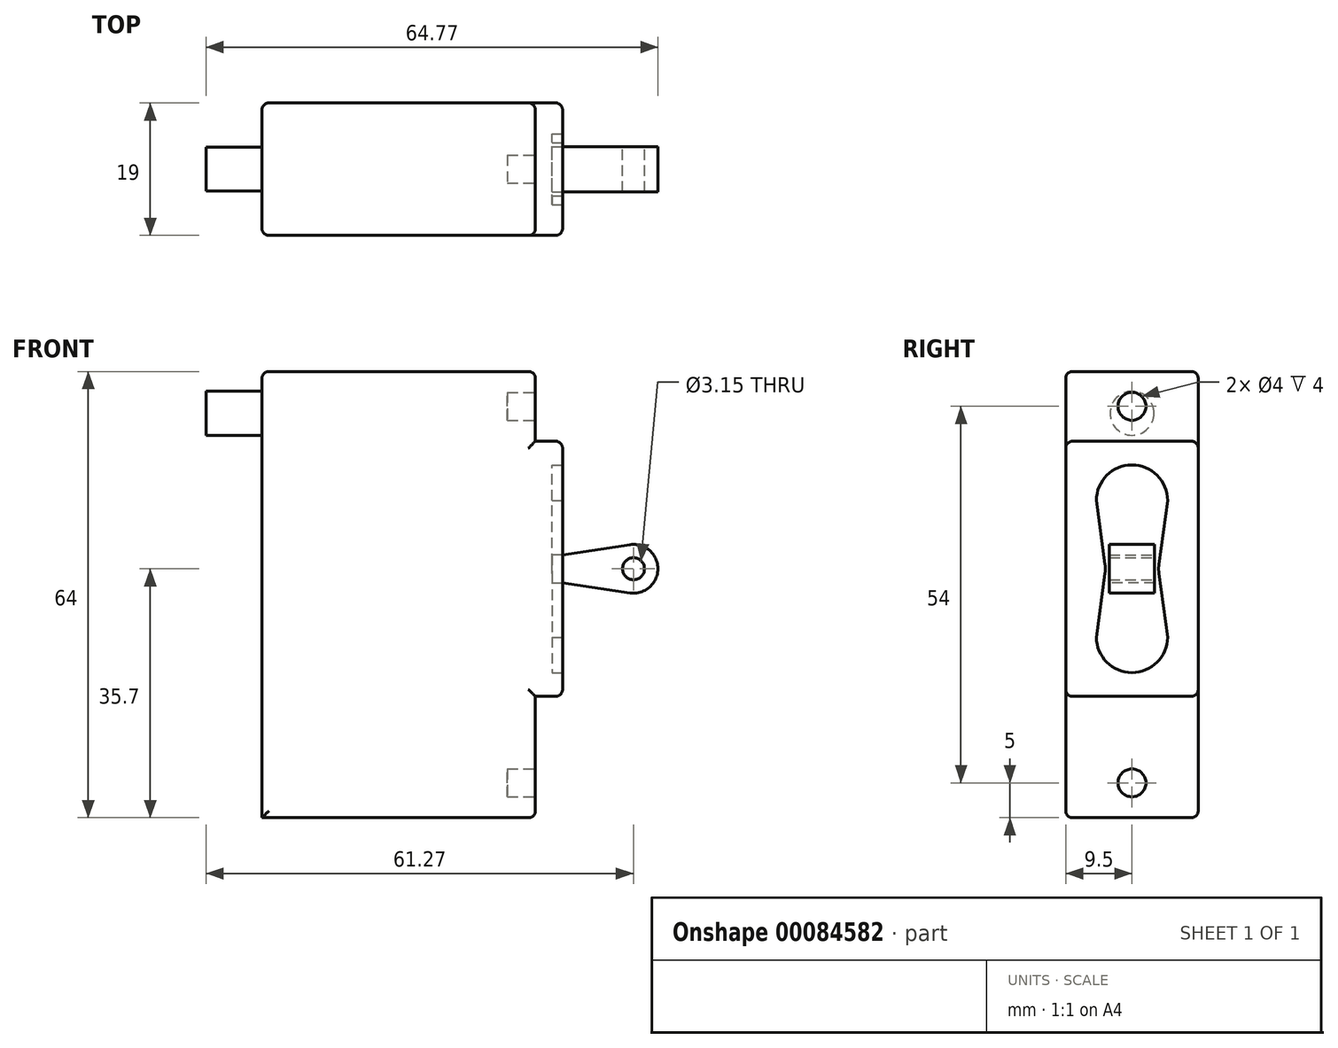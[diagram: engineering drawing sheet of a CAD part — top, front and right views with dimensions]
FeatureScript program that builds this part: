
annotation { "Feature Type Name" : "Feature", "Feature Type Description" : "" }
export const myFeature = defineFeature(function(context is Context, id is Id, definition is map)
    precondition{}
    {
        {
            var Q0;
            Q0=qCreatedBy(makeId("Front.planeOp"),FACE);
            var sketch = newSketch(context, id + "F0", { "sketchPlane" : qUnion([Q0]) });
            skLineSegment(sketch, "E0.bottom", {"start": v(23.6, -32) * mm, "end": v(-23.6, -32) * mm});
            skLineSegment(sketch, "E0.top", {"start": v(23.6, 32) * mm, "end": v(-23.6, 32) * mm});
            skLineSegment(sketch, "E0.left", {"start": v(23.6, -32) * mm, "end": v(23.6, 32) * mm});
            skLineSegment(sketch, "E0.right", {"start": v(-23.6, -32) * mm, "end": v(-23.6, 32) * mm});
            skPoint(sketch, "E0.middle", {"position": v(0, 0) * mm});
            skSolve(sketch);
        }
        {
            var Q0;
            Q0 = qSketchRegion(id + "F0", true);
            extrude(context, id + "F1", {"entities" : qUnion([Q0]), "endBound" : BoundingType.SYMMETRIC, "depth" : 19 * mm});
        }
        {
            var Q0;
            Q0=makeQuery(id+"F1.opExtrude","SWEPT_FACE",FACE,{"disambiguationData":[OSD([sQuery(id+"F0.wireOp",EDGE,"E0.left")])]});
            var sketch = newSketch(context, id + "F2", { "sketchPlane" : qUnion([Q0]) });
            skLineSegment(sketch, "E1", {"start": v(-9.5, 22) * mm, "end": v(9.5, 22) * mm});
            skLineSegment(sketch, "E2.0", {"start": v(-9.5, -14.6) * mm, "end": v(-9.5, 22) * mm});
            skLineSegment(sketch, "E2.1", {"start": v(9.5, -14.6) * mm, "end": v(9.5, 22) * mm});
            skLineSegment(sketch, "E3", {"start": v(-9.5, -14.6) * mm, "end": v(9.5, -14.6) * mm});
            skPoint(sketch, "E4.orphan", {"position": v(-9.5, 32) * mm});
            skPoint(sketch, "E5.orphan", {"position": v(9.5, 32) * mm});
            skPoint(sketch, "E6.orphan", {"position": v(9.5, -32) * mm});
            skPoint(sketch, "E7.orphan", {"position": v(-9.5, -32) * mm});
            skSolve(sketch);
        }
        {
            var Q0;
            Q0 = qSketchRegion(id + "F2", true);
            extrude(context, id + "F3", {"entities" : qUnion([Q0]), "operationType" : NewBodyOperationType.ADD, "depth" : 3.9 * mm});
        }
        {
            var Q0;
            Q0=makeQuery(id+"F3.opExtrude","CAP_FACE",FACE,{"disambiguationData":[OSD([sQuery(id+"F2.wireOp",EDGE,"E1"),sQuery(id+"F2.wireOp",EDGE,"E2.0"),sQuery(id+"F2.wireOp",EDGE,"E2.1"),sQuery(id+"F2.wireOp",EDGE,"E3")])],"isStart":false});
            var sketch = newSketch(context, id + "F4", { "sketchPlane" : qUnion([Q0]) });
            skLineSegment(sketch, "E8", {"start": v(-9.5, 3.7) * mm, "end": v(9.5, 3.7) * mm, "construction": true});
            skLineSegment(sketch, "E9", {"start": v(-9.5, 18.6) * mm, "end": v(9.5, 18.6) * mm, "construction": true});
            skLineSegment(sketch, "E10", {"start": v(3.87, 4.37) * mm, "end": v(5.1, 13.5) * mm});
            skArc(sketch, "E11", {"start": v(0, 18.6) * mm, "mid": v(3.6, 17.1) * mm, "end": v(5.1, 13.5) * mm});
            skArc(sketch, "E12.MirrorCS", {"start": v(0, 18.6) * mm, "mid": v(-3.6, 17.1) * mm, "end": v(-5.1, 13.5) * mm});
            skLineSegment(sketch, "E13.MirrorCS", {"start": v(-3.87, 4.37) * mm, "end": v(-5.1, 13.5) * mm});
            skLineSegment(sketch, "E14.MirrorCS", {"start": v(3.87, 3.03) * mm, "end": v(5.1, -6.1) * mm});
            skArc(sketch, "E15.MirrorCS", {"start": v(0, -11.2) * mm, "mid": v(3.6, -9.7) * mm, "end": v(5.1, -6.1) * mm});
            skArc(sketch, "E16.MirrorCS", {"start": v(0, -11.2) * mm, "mid": v(-3.6, -9.7) * mm, "end": v(-5.1, -6.1) * mm});
            skLineSegment(sketch, "E17.MirrorCS", {"start": v(-3.87, 3.03) * mm, "end": v(-5.1, -6.1) * mm});
            skPoint(sketch, "E18.visualSharp", {"position": v(3.78, 3.7) * mm});
            skArc(sketch, "E18.filletArc", {"start": v(3.87, 4.37) * mm, "mid": v(3.82, 3.7) * mm, "end": v(3.87, 3.03) * mm});
            skPoint(sketch, "E19.visualSharp", {"position": v(-3.78, 3.7) * mm});
            skArc(sketch, "E19.filletArc", {"start": v(-3.87, 3.03) * mm, "mid": v(-3.82, 3.7) * mm, "end": v(-3.87, 4.37) * mm});
            skSolve(sketch);
        }
        {
            var Q0;
            Q0 = qSketchRegion(id + "F4", true);
            extrude(context, id + "F5", {"entities" : qUnion([Q0]), "operationType" : NewBodyOperationType.REMOVE, "oppositeDirection" : true, "depth" : 1.5 * mm});
        }
        {
            var Q0;
            Q0=makeQuery(id+"F1.opExtrude","SWEPT_FACE",FACE,{"disambiguationData":[OSD([sQuery(id+"F0.wireOp",EDGE,"E0.right")])]});
            var sketch = newSketch(context, id + "F6", { "sketchPlane" : qUnion([Q0]) });
            skLineSegment(sketch, "E20", {"start": v(-9.5, -26) * mm, "end": v(9.5, -26) * mm, "construction": true});
            skCircle(sketch, "E21", {"center": v(0, -26) * mm, "radius": 3.15 * mm});
            skCircle(sketch, "E22.MirrorC", {"center": v(0, 26) * mm, "radius": 3.15 * mm});
            skSolve(sketch);
        }
        {
            var Q0;
            Q0=makeQuery(id+"F6.imprint","IMPRINT",FACE,{"disambiguationData":[TD([[makeQuery(id+"F6.imprint","IMPRINT",EDGE,{"derivedFrom":sQuery(id+"F6.wireOp",EDGE,"E22.MirrorC")}),-1.0]])]});
            var Q1;
            Q1=makeQuery(id+"F6.imprint","IMPRINT",FACE,{"disambiguationData":[TD([[makeQuery(id+"F6.imprint","IMPRINT",EDGE,{"derivedFrom":sQuery(id+"F6.wireOp",EDGE,"E21")}),1.0]])]});
            extrude(context, id + "F7", {"entities" : qUnion([Q0, Q1]), "operationType" : NewBodyOperationType.REMOVE, "oppositeDirection" : true, "depth" : 8 * mm});
        }
        {
            var Q0;
            {var subQ1=sQuery(id+"F0.wireOp",EDGE,"E0.left");var subQ2=sQuery(id+"F0.wireOp",EDGE,"E0.top");Q0=makeQuery(id+"F3.boolean.opBoolean","SPLIT",FACE,{"disambiguationData":[TD([makeQuery(id+"F1.opExtrude","SWEPT_FACE",FACE,{"disambiguationData":[OSD([subQ2])]})])],"derivedFrom":makeQuery(id+"F1.opExtrude","SWEPT_FACE",FACE,{"disambiguationData":[OSD([subQ1])]})});}
            var sketch = newSketch(context, id + "F8", { "sketchPlane" : qUnion([Q0]) });
            skCircle(sketch, "E23", {"center": v(0, 27) * mm, "radius": 2 * mm});
            skPoint(sketch, "E23.centerSnap0", {"position": v(-9.5, 27) * mm});
            skCircle(sketch, "E24.MirrorC", {"center": v(0, -27) * mm, "radius": 2 * mm});
            skSolve(sketch);
        }
        {
            var Q0;
            Q0 = qSketchRegion(id + "F8", true);
            extrude(context, id + "F9", {"entities" : qUnion([Q0]), "operationType" : NewBodyOperationType.REMOVE, "oppositeDirection" : true, "depth" : 4 * mm});
        }
        {
            var Q0;
            Q0=qCreatedBy(makeId("Front.planeOp"),FACE);
            var sketch = newSketch(context, id + "F10", { "sketchPlane" : qUnion([Q0]) });
            skPoint(sketch, "E25.0", {"position": v(27.5, 3.7) * mm});
            skLineSegment(sketch, "E26", {"start": v(27.5, 3.7) * mm, "end": v(35.82, 3.7) * mm, "construction": true});
            skCircle(sketch, "E27", {"center": v(37.67, 3.7) * mm, "radius": 1.57 * mm});
            skCircle(sketch, "E28", {"center": v(37.67, 3.7) * mm, "radius": 3.5 * mm});
            skLineSegment(sketch, "E29", {"start": v(27.5, 5.7) * mm, "end": v(37.15, 7.16) * mm});
            skLineSegment(sketch, "E30.MirrorCS", {"start": v(27.5, 1.7) * mm, "end": v(37.15, 0.24) * mm});
            skLineSegment(sketch, "E31", {"start": v(27.5, 5.7) * mm, "end": v(25.5, 5.7) * mm});
            skLineSegment(sketch, "E32", {"start": v(25.5, 5.7) * mm, "end": v(25.5, 1.7) * mm});
            skLineSegment(sketch, "E33", {"start": v(25.5, 1.7) * mm, "end": v(27.5, 1.7) * mm});
            skSolve(sketch);
        }
        {
            var Q0;
            Q0 = qSketchRegion(id + "F10", true);
            extrude(context, id + "F11", {"entities" : qUnion([Q0]), "operationType" : NewBodyOperationType.ADD, "endBound" : BoundingType.SYMMETRIC, "depth" : 6.5 * mm});
        }
        {
            var Q0;
            Q0=makeQuery(id+"F3.boolean.opBoolean","MERGE",FACE,{"derivedFrom":[makeQuery(id+"F1.opExtrude","CAP_FACE",FACE,{"disambiguationData":[OSD([sQuery(id+"F0.wireOp",EDGE,"E0.bottom"),sQuery(id+"F0.wireOp",EDGE,"E0.top"),sQuery(id+"F0.wireOp",EDGE,"E0.left"),sQuery(id+"F0.wireOp",EDGE,"E0.right")])],"isStart":true}),makeQuery(id+"F3.opExtrude","SWEPT_FACE",FACE,{"disambiguationData":[OSD([sQuery(id+"F2.wireOp",EDGE,"E2.1")])]})]});
            var Q1;
            Q1=makeQuery(id+"F1.opExtrude","SWEPT_FACE",FACE,{"disambiguationData":[OSD([sQuery(id+"F0.wireOp",EDGE,"E0.top")])]});
            var Q2;
            Q2=makeQuery(id+"F3.boolean.opBoolean","MERGE",FACE,{"derivedFrom":[makeQuery(id+"F1.opExtrude","CAP_FACE",FACE,{"disambiguationData":[OSD([sQuery(id+"F0.wireOp",EDGE,"E0.bottom"),sQuery(id+"F0.wireOp",EDGE,"E0.top"),sQuery(id+"F0.wireOp",EDGE,"E0.left"),sQuery(id+"F0.wireOp",EDGE,"E0.right")])],"isStart":false}),makeQuery(id+"F3.opExtrude","SWEPT_FACE",FACE,{"disambiguationData":[OSD([sQuery(id+"F2.wireOp",EDGE,"E2.0")])]})]});
            var Q3;
            Q3=makeQuery(id+"F3.opExtrude","CAP_EDGE",EDGE,{"disambiguationData":[OSD([sQuery(id+"F2.wireOp",EDGE,"E3")])],"isStart":false});
            var Q4;
            Q4=makeQuery(id+"F3.opExtrude","CAP_EDGE",EDGE,{"disambiguationData":[OSD([sQuery(id+"F2.wireOp",EDGE,"E1")])],"isStart":false});
            var Q5;
            Q5=makeQuery(id+"F1.opExtrude","SWEPT_EDGE",EDGE,{"disambiguationData":[OSD([sQuery(id+"F0.wireOp",EDGE,"E0.bottom"),sQuery(id+"F0.wireOp",EDGE,"E0.left")])]});
            var Q6;
            Q6=makeQuery(id+"F1.opExtrude","SWEPT_EDGE",EDGE,{"disambiguationData":[OSD([sQuery(id+"F0.wireOp",EDGE,"E0.bottom"),sQuery(id+"F0.wireOp",EDGE,"E0.right")])]});
            fillet(context, id + "F12", {"entities" : qUnion([Q0, Q1, Q2, Q3, Q4, Q5, Q6]), "radius" : 1 * mm, "tangentPropagation" : true, "conicFillet" : false});
        }
    });
